# Revit family: Building-SurfaceMountingEnclosures-GEWISS-44CE-JUNCTION-BOXES-WALL-MOUNTING_6HOLES
name_source: partatom
category: Apparecchi elettrici
revit_build: Autodesk Revit 2016 (Build: 20161004_0715(x64)
units: mm (PartAtom-declared; Revit-internal decimal feet)

## family parameters
Condiviso = No
Host = Superficie
Mantenere orientamento annotazione = Sì
Numero OmniClass = 23.80.30.14.24
Punto di calcolo locali = Sì
Quota connettore circolare = Usa diametro
Taglio con vuoti quando caricato = No
Tipo di parte = Normale
Titolo OmniClass = Junction Boxes

## types (1)
- Building-SurfaceMountingEnclosures-GEWISS-44CE-JUNCTION-BOXES-WALL-MOUNTING_6HOLES
    Accessories for insulation restoring = GW44622
    Application = Special uses
    Carico apparente = 0 VA
    Catalogue = BUILDING
    Catalogue Range = 44 CE
    Classificazione = Other
    Colour = Grey RAL 7035
    Coperchio = GEWISS COPERCHIO
    Descrizione = JUNCT.BOX GL.120X80X50 IP55 GWT960
    Diametro = 28 mm  [stored 0.0918635 ft]
    Distanza fori = 34 mm  [stored 0.111549 ft]
    EAN code = 8011564243835
    Electrocod = 02210
    Elemento di dettaglio = Dettaglio - 44CE-6IN : 120x80x50
    Entries No. holes / Ã˜ = 6 / 29
    Glow Wire Test = 960°C
    IDF = 18d25195-dea2-4b78-b902-1f567c73e7c4
    IDT = 20642058-6ce6-487d-a89f-98600aa2adb7
    IP degree = IP55
    Immagine tipo = GW44055.jpg
    Insulation class = II (according to IEC 61140 standards)
    Internal dim. LxHxD (mm) = 120x80x50
    Larghezza = 120 mm  [stored 0.393701 ft]
    Lid = Plain screwed
    Lid screws (no. and type) = 4 - Stainless steel
    Lunghezza = 80 mm  [stored 0.262467 ft]
    Material = Technopolymer GWPLAST 75
    Modello = GW44055
    Operating temperature = -25 +60 °C
    Produttore = GEWISS S.p.A.
    Prospetto di default = 1219 mm
    Raggio = 14 mm  [stored 0.0459318 ft]
    SEO = Box
    Scatola = GEWISS SCATOLA
    Shock resistance = IK08
    Spessore = 50 mm  [stored 0.164042 ft]
    Technical sheet = https://www.gewiss.com
    Thermo-pressure with ball = 85
    Torque screws tightening = 1NM
    URL = https://www.gewiss.com
    Version file RFA = 18.0
    Voltaggio_x = 0 V
    Walls = With cable glands

note: source unit labels omitted for Thermo-pressure with ball — the stored unit's dimension contradicts the parameter name (converter mislabeling)

note: [stored X ft] marks values corroborated as IEEE doubles in the binary element streams (Revit-internal decimal feet)

## geometry (parser evidence)
native form markers: Blend x2, Sweep x1
no freeform markers — native parametric forms only
